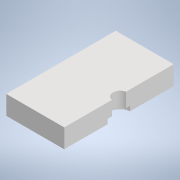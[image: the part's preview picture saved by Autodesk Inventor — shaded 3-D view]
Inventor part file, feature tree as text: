
AUTODESK INVENTOR PART (.ipt)
format: ipt  version: 2020 (Build 240168000, 168)  size: 131,584 bytes
history: native  units: mm
features: extrude x4, sketch x4
ambient origin geometry x8: Origin, YZ Plane, XZ Plane, XY Plane, X Axis, Y Axis, Z Axis, Center Point
bodies: Solido1 (feature_tree)
feature tree (8):
  extrude  "Estrusione1"  Depth=19.0mm
  extrude  "Estrusione2"  Depth=16.0mm TaperAngle=0.0deg
  extrude  "Estrusione3"  Depth=4.0mm TaperAngle=0.0deg
  extrude  "Estrusione4"  Depth=26.0mm TaperAngle=0.0deg
  sketch  "Schizzo1"
  sketch  "Schizzo2"
  sketch  "Schizzo4"
  sketch  "Schizzo8"
